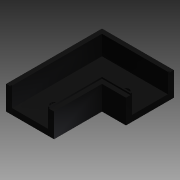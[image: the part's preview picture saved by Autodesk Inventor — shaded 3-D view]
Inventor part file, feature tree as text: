
AUTODESK INVENTOR PART (.ipt)
format: ipt  version: 2014 (Build 180170000, 170)  size: 163,840 bytes
history: native  units: in
note: dims shown in document units (in); Inventor stores cm internally (conversion verified against a paired STEP export)
features: extrude x5, sketch x5, other x2, split x1
ambient origin geometry x8: Origin, YZ Plane, XZ Plane, XY Plane, X Axis, Y Axis, Z Axis, Center Point
bodies: Solid1 (feature_tree)
feature tree (13):
  extrude  "Extrusion1"  Depth=1.0in
  extrude  "Extrusion2"  Depth=0.5in TaperAngle=0.0deg
  extrude  "Extrusion4"  Depth=0.75in
  extrude  "Extrusion5"  Depth=0.75in
  extrude  "Extrusion6"  Depth=0.03in TaperAngle=0.0deg
  split  "Split2"
  other  "Lip4"
  other  "Lip5"
  sketch  "Sketch1"  dims[d0=1.0in d1=1.0in]
  sketch  "Sketch2"  dims[d2=2.0in d3=0.0in d4=0.5in d5=0.0in]
  sketch  "Sketch5"  dims[d8=0.75in d9=0.75in]
  sketch  "Sketch6"  dims[d10=1.75in d11=0.0in d12=0.75in]
  sketch  "Sketch7"  dims[d13=0.75in d14=1.75in d15=0.0in d34=0.141in d35=1.0in d36=0.0in d38=0.03in d39=0.03in d40=0.0in d41=0.0in d42=0.0in d43=0.0in d44=0.03in d45=0.03in d46=0.0in d47=0.0in d48=0.0in d49=0.0in]
